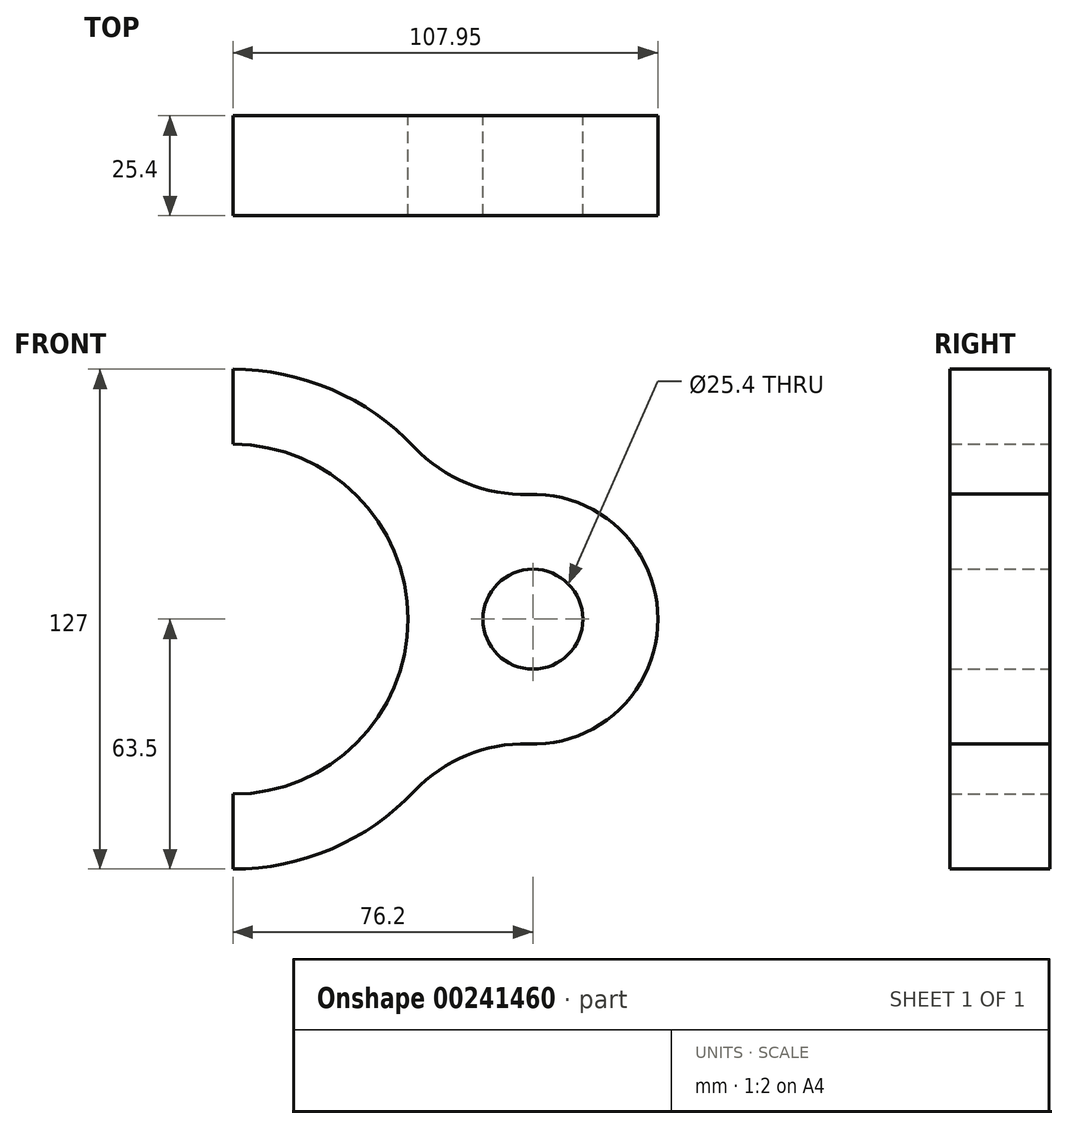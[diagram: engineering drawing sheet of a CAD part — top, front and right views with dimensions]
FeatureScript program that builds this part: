
annotation { "Feature Type Name" : "Feature", "Feature Type Description" : "" }
export const myFeature = defineFeature(function(context is Context, id is Id, definition is map)
    precondition{}
    {
        {
            var Q0;
            Q0=qCreatedBy(makeId("Front.planeOp"),FACE);
            var sketch = newSketch(context, id + "F0", { "sketchPlane" : qUnion([Q0])});
            skCircle(sketch, "E0", {"center": v(0, 0) * mm, "radius": 44.45 * mm});
            skArc(sketch, "E1", {"start": v(46.14, 43.63) * mm, "mid": v(0, 63.5) * mm, "end": v(-46.14, 43.63) * mm});
            skArc(sketch, "E2", {"start": v(75.12, -31.73) * mm, "mid": v(107.95, 0) * mm, "end": v(75.12, 31.73) * mm});
            skCircle(sketch, "E3", {"center": v(76.2, 0) * mm, "radius": 12.7 * mm});
            skPoint(sketch, "E4.visualSharp", {"position": v(57.94, 25.98) * mm});
            skArc(sketch, "E4.filletArc", {"start": v(46.14, 43.63) * mm, "mid": v(59.35, 34.56) * mm, "end": v(75.12, 31.73) * mm});
            skPoint(sketch, "E5.visualSharp", {"position": v(57.94, -25.98) * mm});
            skArc(sketch, "E5.filletArc", {"start": v(75.12, -31.73) * mm, "mid": v(59.35, -34.56) * mm, "end": v(46.14, -43.63) * mm});
            skLineSegment(sketch, "E6", {"start": v(0, 71.67) * mm, "end": v(0, -73.16) * mm});
            skArc(sketch, "E7.MirrorCS", {"start": v(-46.14, 43.63) * mm, "mid": v(-59.35, 34.56) * mm, "end": v(-75.12, 31.73) * mm});
            skArc(sketch, "E8.MirrorCS", {"start": v(-75.12, -31.73) * mm, "mid": v(-107.95, 0) * mm, "end": v(-75.12, 31.73) * mm});
            skCircle(sketch, "E9.MirrorC", {"center": v(-76.2, 0) * mm, "radius": 12.7 * mm});
            skArc(sketch, "E10.MirrorCS", {"start": v(-75.12, -31.73) * mm, "mid": v(-59.35, -34.56) * mm, "end": v(-46.14, -43.63) * mm});
            skArc(sketch, "E11.trimOffspring", {"start": v(-46.14, -43.63) * mm, "mid": v(0, -63.5) * mm, "end": v(46.14, -43.63) * mm});
            skSolve(sketch);
        }
        {
            var Q0;
            {var subQ5=sQuery(id+"F0.wireOp",EDGE,"E7.MirrorCS");Q0=makeQuery(id+"F0.imprint","IMPRINT",FACE,{"disambiguationData":[TD([[makeQuery(id+"F0.imprint","IMPRINT",EDGE,{"derivedFrom":subQ5}),1.0]])]});}
            var Q1;
            Q1=makeQuery(id+"F0.imprint","IMPRINT",FACE,{"disambiguationData":[TD([[makeQuery(id+"F0.imprint","IMPRINT",EDGE,{"derivedFrom":sQuery(id+"F0.wireOp",EDGE,"E2")}),1.0]])]});
            extrude(context, id + "F1", {"entities" : qUnion([Q0, Q1]), "depth" : 25.4 * mm});
        }
    });
